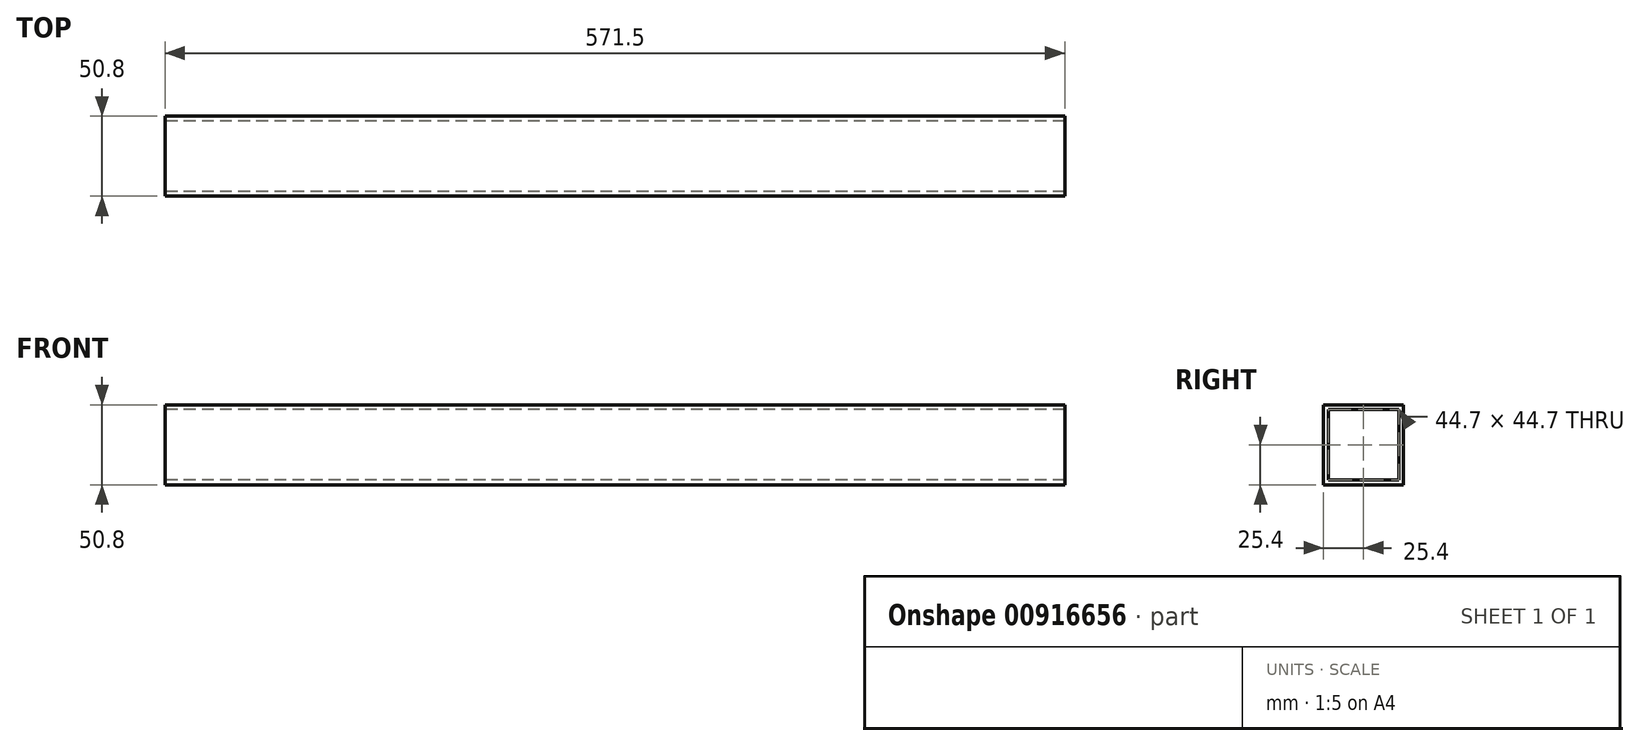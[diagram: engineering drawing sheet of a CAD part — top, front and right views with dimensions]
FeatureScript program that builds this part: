
annotation { "Feature Type Name" : "Feature", "Feature Type Description" : "" }
export const myFeature = defineFeature(function(context is Context, id is Id, definition is map)
    precondition{}
    {
        {
            var Q0;
            Q0=qCreatedBy(makeId("Right.planeOp"),FACE);
            var sketch = newSketch(context, id + "F0", { "sketchPlane" : qUnion([Q0])});
            skLineSegment(sketch, "E0.bottom", {"start": v(25.4, 25.4) * mm, "end": v(-25.4, 25.4) * mm});
            skLineSegment(sketch, "E0.top", {"start": v(25.4, -25.4) * mm, "end": v(-25.4, -25.4) * mm});
            skLineSegment(sketch, "E0.left", {"start": v(25.4, 25.4) * mm, "end": v(25.4, -25.4) * mm});
            skLineSegment(sketch, "E0.right", {"start": v(-25.4, 25.4) * mm, "end": v(-25.4, -25.4) * mm});
            skPoint(sketch, "E0.middle", {"position": v(0, 0) * mm});
            skLineSegment(sketch, "E1.bottom", {"start": v(-22.35, 22.35) * mm, "end": v(22.35, 22.35) * mm});
            skLineSegment(sketch, "E1.top", {"start": v(-22.35, -22.35) * mm, "end": v(22.35, -22.35) * mm});
            skLineSegment(sketch, "E1.left", {"start": v(-22.35, 22.35) * mm, "end": v(-22.35, -22.35) * mm});
            skLineSegment(sketch, "E1.right", {"start": v(22.35, 22.35) * mm, "end": v(22.35, -22.35) * mm});
            skSolve(sketch);
        }
        {
            var Q0;
            Q0=qSketchRegion(id+"F0",true);
            extrude(context, id + "F1", {"entities" : qUnion([Q0]), "depth" : 571.5 * mm, "offsetDistance" : 25.4 * mm});
        }
    });
